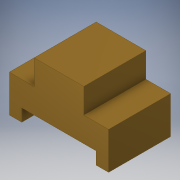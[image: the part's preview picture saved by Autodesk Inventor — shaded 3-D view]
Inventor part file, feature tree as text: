
AUTODESK INVENTOR PART (.ipt)
format: ipt  version: 2017 (Build 210142000, 142)  size: 104,448 bytes
history: native  units: in
note: dims shown in document units (in); Inventor stores cm internally (conversion verified against a paired STEP export)
features: extrude x1, sketch x1
ambient origin geometry x8: Origin, YZ Plane, XZ Plane, XY Plane, X Axis, Y Axis, Z Axis, Center Point
bodies: Solid1 (feature_tree)
feature tree (2):
  extrude  "Extrusion1"  Depth=0.25in
  sketch  "Sketch1"  dims[d1=0.25in d2=0.25in d3=1.5in d4=0.25in d5=0.75in d6=0.5in d7=0.5in d8=1.0in d9=1.25in d10=0.0in]
